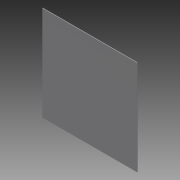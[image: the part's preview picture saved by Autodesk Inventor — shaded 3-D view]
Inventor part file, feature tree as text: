
AUTODESK INVENTOR PART (.ipt)
format: ipt  version: 2013 (Build 170138000, 138)  size: 68,096 bytes
history: native  units: in
note: dims shown in document units (in); Inventor stores cm internally (conversion verified against a paired STEP export)
features: extrude x1, sketch x1
ambient origin geometry x8: Origin, YZ Plane, XZ Plane, XY Plane, X Axis, Y Axis, Z Axis, Center Point
bodies: Solid1 (feature_tree)
feature tree (2):
  extrude  "Extrusion1"  Depth=24.0in
  sketch  "Sketch1"  dims[d0=24.0in d1=24.0in d2=0.12in d3=0.0in]
